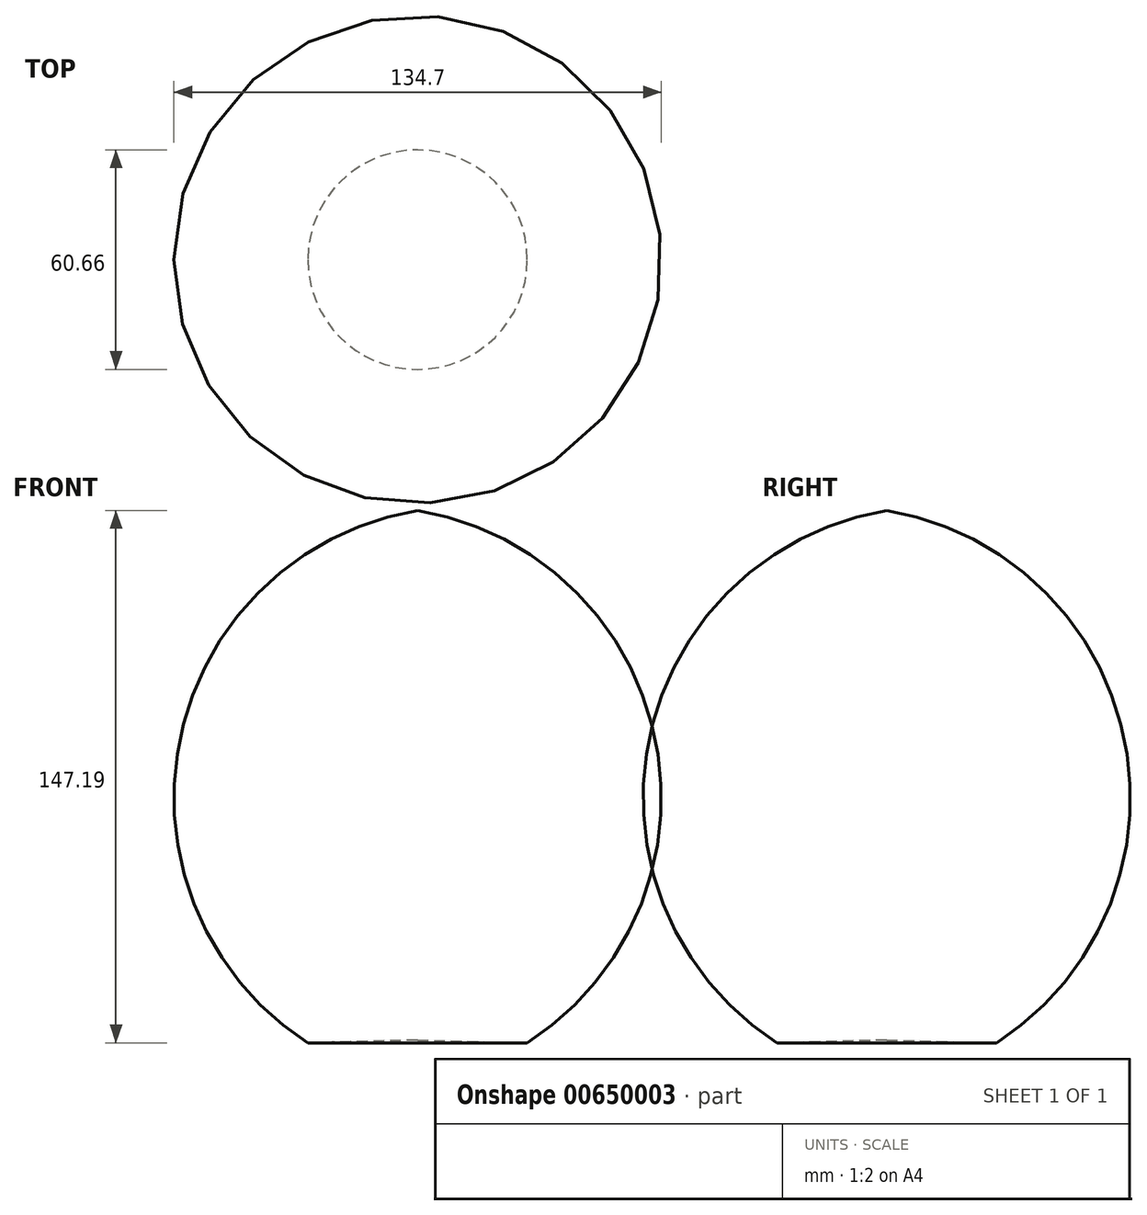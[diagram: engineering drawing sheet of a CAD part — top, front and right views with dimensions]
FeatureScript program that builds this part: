
annotation { "Feature Type Name" : "Feature", "Feature Type Description" : "" }
export const myFeature = defineFeature(function(context is Context, id is Id, definition is map)
    precondition{}
    {
        {
            var Q0;
            Q0=qCreatedBy(makeId("Front.planeOp"),FACE);
            var sketch = newSketch(context, id + "F0", { "sketchPlane" : qUnion([Q0])});
            skLineSegment(sketch, "E0", {"start": v(9.28, -51.57) * mm, "end": v(-21.05, -50.82) * mm});
            skArc(sketch, "E1", {"start": v(9.28, -51.57) * mm, "mid": v(44.64, 32.44) * mm, "end": v(-21.05, 95.62) * mm});
            skLineSegment(sketch, "E2", {"start": v(-21.05, 95.62) * mm, "end": v(-21.05, -50.82) * mm});
            skSolve(sketch);
        }
        {
            var Q0;
            Q0 = qSketchRegion(id + "F0", true);
            var Q1;
            Q1=sQuery(id+"F0.wireOp",EDGE,"E2");
            revolve(context, id + "F1", {"entities" : qUnion([Q0]), "axis" : qUnion([Q1]), "revolveType" : RevolveType.FULL});
        }
    });
